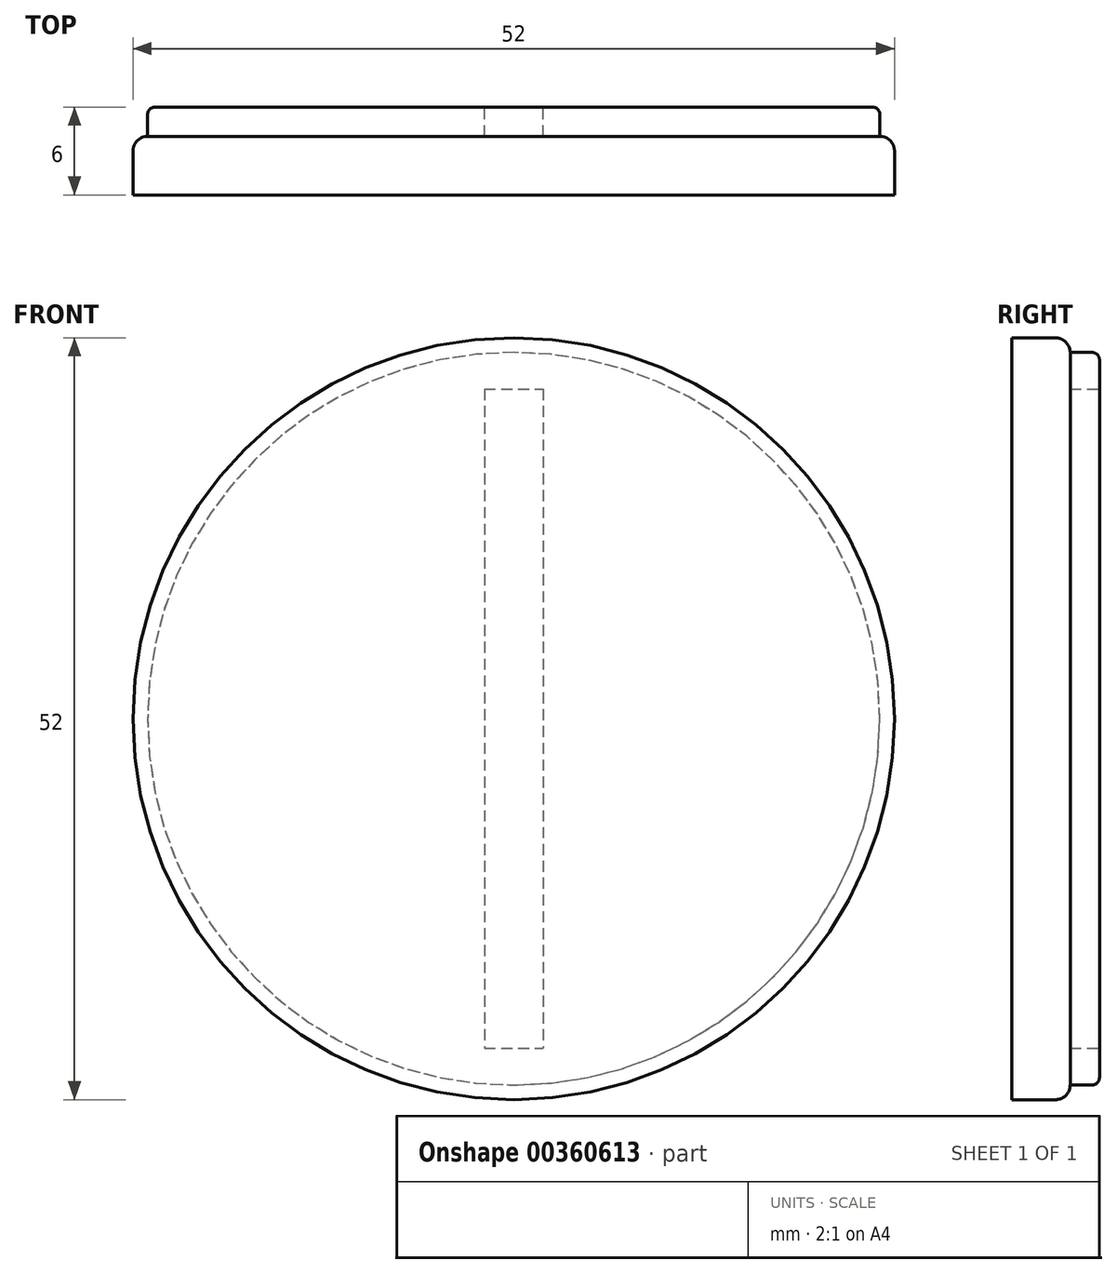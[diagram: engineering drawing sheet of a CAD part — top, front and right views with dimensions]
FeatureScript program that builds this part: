
annotation { "Feature Type Name" : "Feature", "Feature Type Description" : "" }
export const myFeature = defineFeature(function(context is Context, id is Id, definition is map)
    precondition{}
    {
        {
            var Q0;
            Q0=qCreatedBy(makeId("Front.planeOp"),FACE);
            var sketch = newSketch(context, id + "F0", { "sketchPlane" : qUnion([Q0])});
            skCircle(sketch, "E0", {"center": v(0, 0) * mm, "radius": 26 * mm});
            skSolve(sketch);
        }
        {
            var Q0;
            Q0=makeQuery(id+"F0.imprint","IMPRINT",FACE,{"disambiguationData":[TD([[makeQuery(id+"F0.imprint","IMPRINT",EDGE,{"derivedFrom":sQuery(id+"F0.wireOp",EDGE,"E0")}),1.0]])]});
            extrude(context, id + "F1", {"entities" : qUnion([Q0]), "depth" : 4 * mm});
        }
        {
            var Q0;
            Q0=makeQuery(id+"F1.opExtrude","CAP_FACE",FACE,{"disambiguationData":[OSD([sQuery(id+"F0.wireOp",EDGE,"E0")])],"isStart":true});
            var sketch = newSketch(context, id + "F2", { "sketchPlane" : qUnion([Q0])});
            skCircle(sketch, "E1", {"center": v(0, 0) * mm, "radius": 25 * mm});
            skSolve(sketch);
        }
        {
            var Q0;
            Q0 = qSketchRegion(id + "F2", true);
            extrude(context, id + "F3", {"entities" : qUnion([Q0]), "operationType" : NewBodyOperationType.ADD, "depth" : 2 * mm});
        }
        {
            var Q0;
            Q0=makeQuery(id+"F1.opExtrude","CAP_EDGE",EDGE,{"disambiguationData":[OSD([sQuery(id+"F0.wireOp",EDGE,"E0")])],"isStart":true});
            fillet(context, id + "F4", {"entities" : qUnion([Q0]), "radius" : 1 * mm, "tangentPropagation" : true, "allowEdgeOverflow" : false});
        }
        {
            var Q0;
            Q0=makeQuery(id+"F3.opExtrude","CAP_EDGE",EDGE,{"disambiguationData":[OSD([sQuery(id+"F2.wireOp",EDGE,"E1")])],"isStart":false});
            fillet(context, id + "F5", {"entities" : qUnion([Q0]), "radius" : 0.5 * mm, "tangentPropagation" : true, "allowEdgeOverflow" : false});
        }
        {
            var Q0;
            Q0=makeQuery(id+"F3.opExtrude","CAP_FACE",FACE,{"disambiguationData":[OSD([sQuery(id+"F2.wireOp",EDGE,"E1")])],"isStart":false});
            var sketch = newSketch(context, id + "F6", { "sketchPlane" : qUnion([Q0])});
            skLineSegment(sketch, "E2.bottom", {"start": v(2, 22.5) * mm, "end": v(-2, 22.5) * mm});
            skLineSegment(sketch, "E2.top", {"start": v(2, -22.5) * mm, "end": v(-2, -22.5) * mm});
            skLineSegment(sketch, "E2.left", {"start": v(2, 22.5) * mm, "end": v(2, -22.5) * mm});
            skLineSegment(sketch, "E2.right", {"start": v(-2, 22.5) * mm, "end": v(-2, -22.5) * mm});
            skPoint(sketch, "E2.middle", {"position": v(0, 0) * mm});
            skSolve(sketch);
        }
        {
            var Q0;
            Q0 = qSketchRegion(id + "F6", true);
            extrude(context, id + "F7", {"entities" : qUnion([Q0]), "operationType" : NewBodyOperationType.REMOVE, "oppositeDirection" : true, "depth" : 2 * mm});
        }
    });
